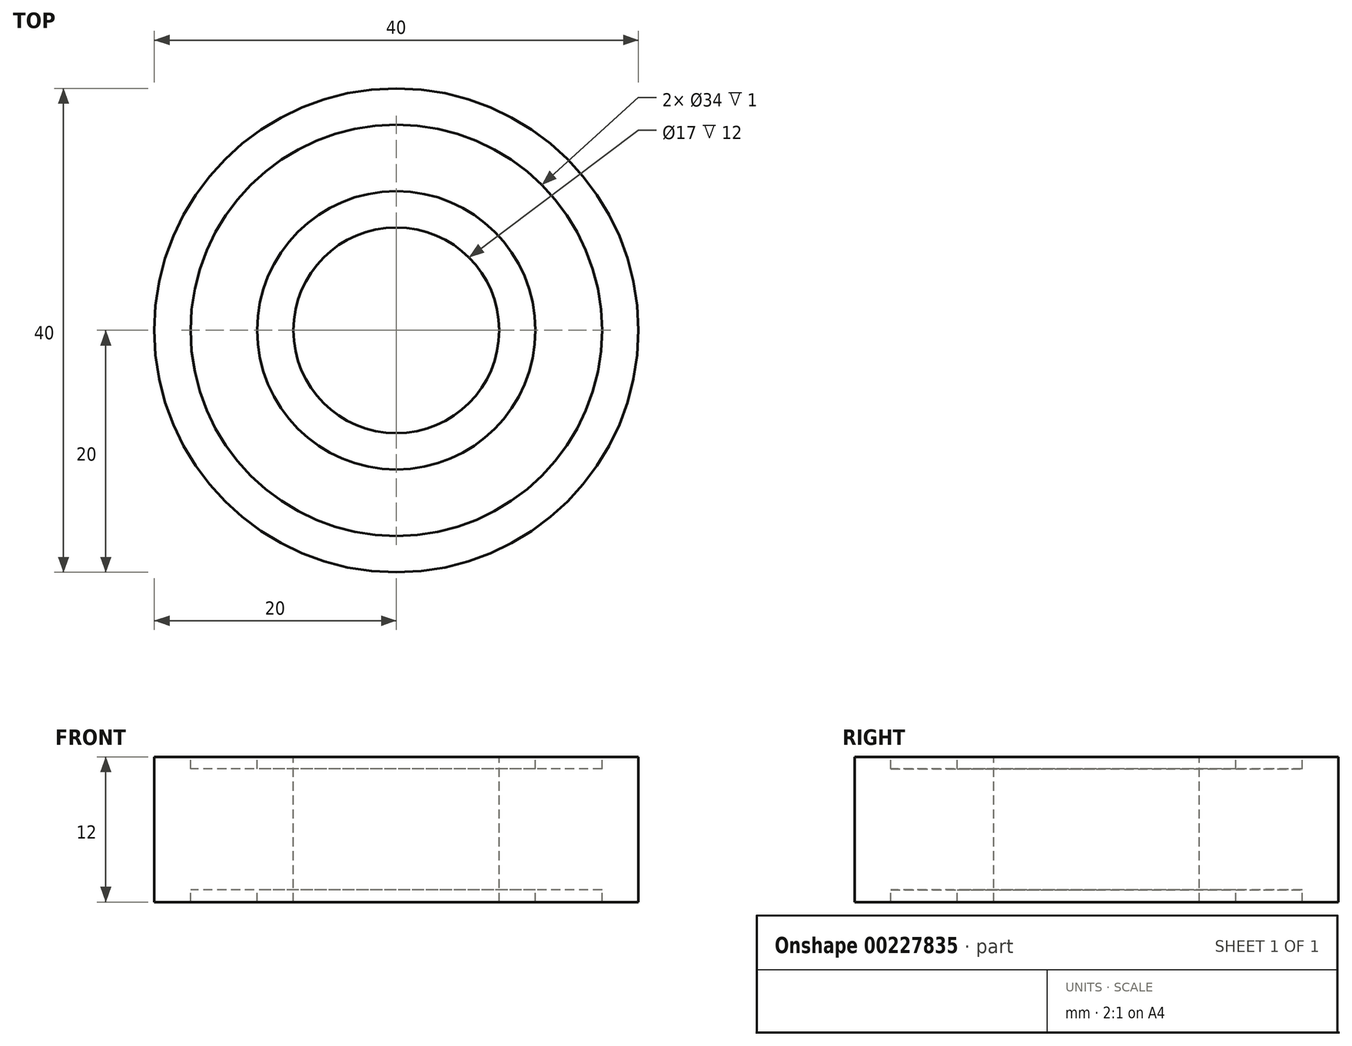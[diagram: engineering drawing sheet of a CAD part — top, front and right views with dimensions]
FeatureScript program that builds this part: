
annotation { "Feature Type Name" : "Feature", "Feature Type Description" : "" }
export const myFeature = defineFeature(function(context is Context, id is Id, definition is map)
    precondition{}
    {
        {
            var Q0;
            Q0=qCreatedBy(makeId("Front.planeOp"),FACE);
            var sketch = newSketch(context, id + "F0", { "sketchPlane" : qUnion([Q0])});
            skLineSegment(sketch, "E0", {"start": v(-20, 6) * mm, "end": v(-20, 0) * mm});
            skLineSegment(sketch, "E1", {"start": v(-20, 6) * mm, "end": v(-17, 6) * mm});
            skLineSegment(sketch, "E2", {"start": v(-8.5, 6) * mm, "end": v(-8.5, 0) * mm});
            skLineSegment(sketch, "E3", {"start": v(-17, 6) * mm, "end": v(-17, 5) * mm});
            skLineSegment(sketch, "E4", {"start": v(-11.5, 6) * mm, "end": v(-11.5, 5) * mm});
            skLineSegment(sketch, "E5", {"start": v(-17, 5) * mm, "end": v(-11.5, 5) * mm});
            skLineSegment(sketch, "E6.trimOffspring", {"start": v(-11.5, 6) * mm, "end": v(-8.5, 6) * mm});
            skPoint(sketch, "E7", {"position": v(0, 0) * mm});
            skLineSegment(sketch, "E8", {"start": v(0, 16.42) * mm, "end": v(0, -13.94) * mm});
            skLineSegment(sketch, "E9", {"start": v(-25, 0) * mm, "end": v(-3.52, 0) * mm, "construction": true});
            skLineSegment(sketch, "E10.MirrorCS", {"start": v(-17, -6) * mm, "end": v(-17, -5) * mm});
            skLineSegment(sketch, "E11.MirrorCS", {"start": v(-11.5, -6) * mm, "end": v(-11.5, -5) * mm});
            skLineSegment(sketch, "E12.MirrorCS", {"start": v(-11.5, -6) * mm, "end": v(-8.5, -6) * mm});
            skLineSegment(sketch, "E13.MirrorCS", {"start": v(-20, -6) * mm, "end": v(-17, -6) * mm});
            skLineSegment(sketch, "E14.MirrorCS", {"start": v(-20, -6) * mm, "end": v(-20, 0) * mm});
            skLineSegment(sketch, "E15.MirrorCS", {"start": v(-17, -5) * mm, "end": v(-11.5, -5) * mm});
            skLineSegment(sketch, "E16.MirrorCS", {"start": v(-8.5, -6) * mm, "end": v(-8.5, 0) * mm});
            skSolve(sketch);
        }
        {
            var Q0;
            Q0=qSketchRegion(id+"F0",true);
            var Q1;
            Q1=sQuery(id+"F0.wireOp",EDGE,"E8");
            revolve(context, id + "F1", {"entities" : qUnion([Q0]), "axis" : qUnion([Q1]), "revolveType" : RevolveType.FULL});
        }
    });
